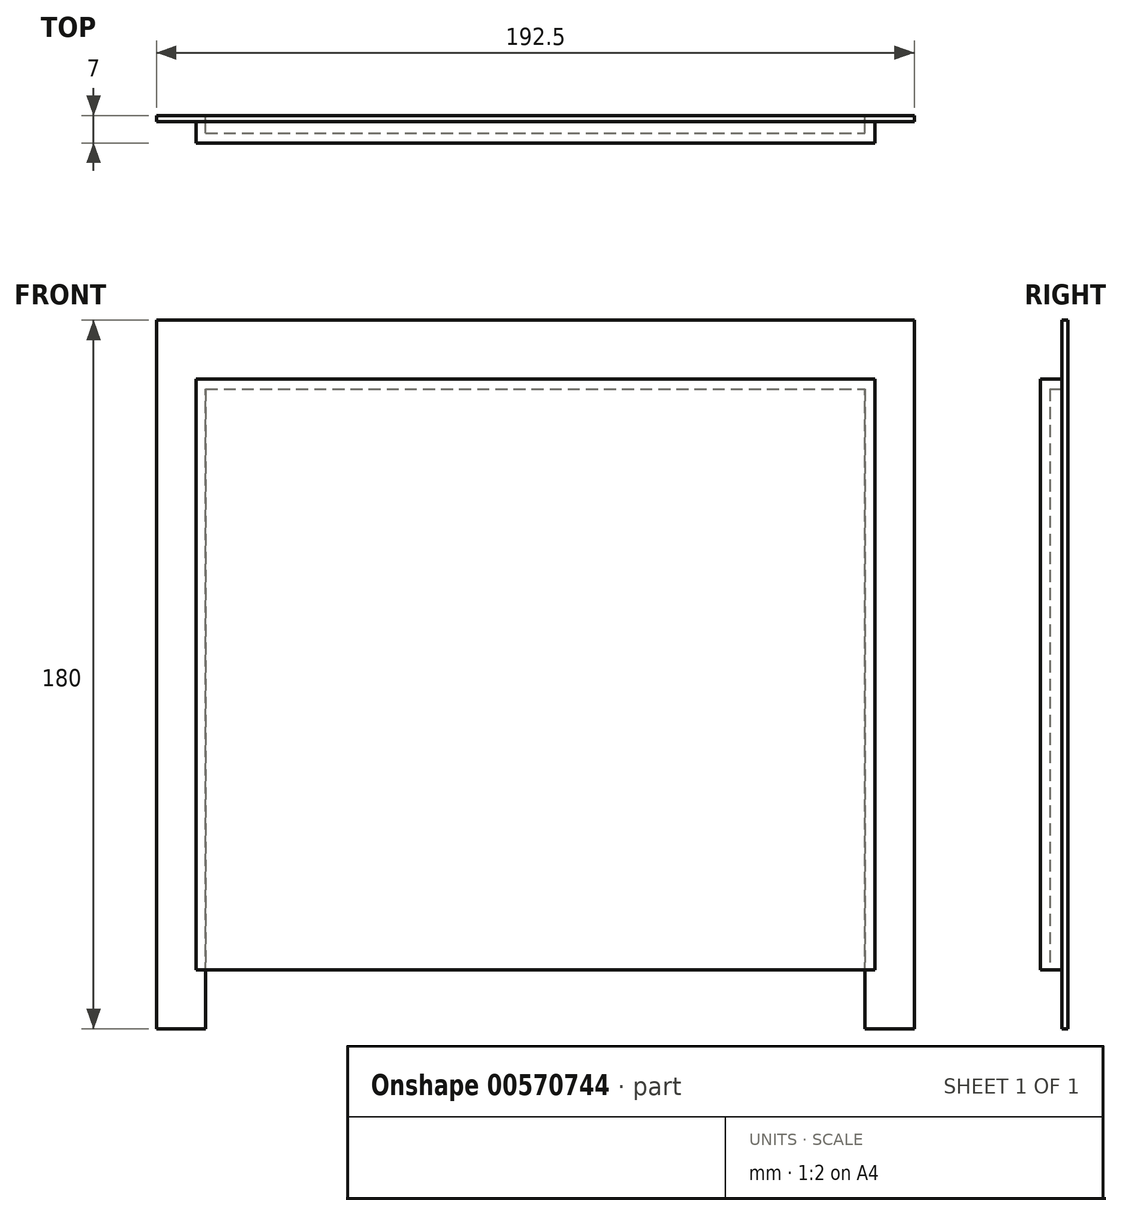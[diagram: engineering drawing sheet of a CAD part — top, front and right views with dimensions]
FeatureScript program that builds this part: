
annotation { "Feature Type Name" : "Feature", "Feature Type Description" : "" }
export const myFeature = defineFeature(function(context is Context, id is Id, definition is map)
    precondition{}
    {
        {
            var Q0;
            Q0=qCreatedBy(makeId("Front.planeOp"),FACE);
            var sketch = newSketch(context, id + "F0", { "sketchPlane" : qUnion([Q0])});
            skLineSegment(sketch, "E0.bottom", {"start": v(96.25, 90) * mm, "end": v(-96.25, 90) * mm});
            skLineSegment(sketch, "E0.top", {"start": v(96.25, -90) * mm, "end": v(-96.25, -90) * mm});
            skLineSegment(sketch, "E0.left", {"start": v(96.25, 90) * mm, "end": v(96.25, -90) * mm});
            skLineSegment(sketch, "E0.right", {"start": v(-96.25, 90) * mm, "end": v(-96.25, -90) * mm});
            skPoint(sketch, "E0.middle", {"position": v(0, 0) * mm});
            skSolve(sketch);
        }
        {
            var Q0;
            Q0=makeQuery(id+"F0.imprint","IMPRINT",FACE,{"disambiguationData":[TD([[makeQuery(id+"F0.imprint","IMPRINT",EDGE,{"derivedFrom":sQuery(id+"F0.wireOp",EDGE,"E0.bottom")}),1.0]])]});
            extrude(context, id + "F1", {"entities" : qUnion([Q0]), "depth" : 1.5 * mm, "offsetDistance" : 25 * mm});
        }
        {
            var Q0;
            Q0=makeQuery(id+"F1.opExtrude","CAP_FACE",FACE,{"disambiguationData":[OSD([sQuery(id+"F0.wireOp",EDGE,"E0.bottom"),sQuery(id+"F0.wireOp",EDGE,"E0.top"),sQuery(id+"F0.wireOp",EDGE,"E0.left"),sQuery(id+"F0.wireOp",EDGE,"E0.right")])],"isStart":false});
            var sketch = newSketch(context, id + "F2", { "sketchPlane" : qUnion([Q0])});
            skLineSegment(sketch, "E1.bottom", {"start": v(86.25, 75) * mm, "end": v(-86.25, 75) * mm});
            skLineSegment(sketch, "E1.top", {"start": v(86.25, -75) * mm, "end": v(-86.25, -75) * mm});
            skLineSegment(sketch, "E1.left", {"start": v(86.25, 75) * mm, "end": v(86.25, -75) * mm});
            skLineSegment(sketch, "E1.right", {"start": v(-86.25, 75) * mm, "end": v(-86.25, -75) * mm});
            skPoint(sketch, "E1.middle", {"position": v(0, 0) * mm});
            skSolve(sketch);
        }
        {
            var Q0;
            Q0 = qSketchRegion(id + "F2", true);
            extrude(context, id + "F3", {"entities" : qUnion([Q0]), "operationType" : NewBodyOperationType.ADD, "depth" : 5.5 * mm, "offsetDistance" : 25 * mm});
        }
        {
            var Q0;
            Q0=makeQuery(id+"F1.opExtrude","CAP_FACE",FACE,{"disambiguationData":[OSD([sQuery(id+"F0.wireOp",EDGE,"E0.bottom"),sQuery(id+"F0.wireOp",EDGE,"E0.top"),sQuery(id+"F0.wireOp",EDGE,"E0.left"),sQuery(id+"F0.wireOp",EDGE,"E0.right")])],"isStart":true});
            shell(context, id + "F4", {"entities" : qUnion([Q0]), "thickness" : 2.5 * mm});
        }
        {
            var Q0;
            Q0=makeQuery(id+"F4.opShell","OFFSET_EDGE",EDGE,{"disambiguationData":[OSD([sQuery(id+"F2.wireOp",EDGE,"E1.top")])]});
            var Q1;
            Q1=makeQuery(id+"F4.opShell","OFFSET_EDGE",EDGE,{"disambiguationData":[OSD([sQuery(id+"F2.wireOp",EDGE,"E1.top"),sQuery(id+"F2.wireOp",EDGE,"E1.left")])]});
            cPlane(context, id + "F5", {"entities" : qUnion([Q0, Q1]), "cplaneType" : CPlaneType.LINE_ANGLE, "offset" : 25 * mm, "angle" : 0 * degree, "width" : 150 * mm, "height" : 150 * mm});
        }
        {
            var Q0;
            Q0=qCreatedBy(id+"F5.planeOp",FACE);
            var sketch = newSketch(context, id + "F6", { "sketchPlane" : qUnion([Q0])});
            skLineSegment(sketch, "E2.bottom", {"start": v(83.75, 0) * mm, "end": v(-83.75, 0) * mm});
            skLineSegment(sketch, "E2.top", {"start": v(83.75, 4.5) * mm, "end": v(-83.75, 4.5) * mm});
            skLineSegment(sketch, "E2.left", {"start": v(83.75, 0) * mm, "end": v(83.75, 4.5) * mm});
            skLineSegment(sketch, "E2.right", {"start": v(-83.75, 0) * mm, "end": v(-83.75, 4.5) * mm});
            skSolve(sketch);
        }
        {
            var Q0;
            Q0 = qSketchRegion(id + "F6", true);
            extrude(context, id + "F7", {"entities" : qUnion([Q0]), "operationType" : NewBodyOperationType.REMOVE, "endBound" : BoundingType.THROUGH_ALL, "depth" : 25 * mm, "offsetDistance" : 25 * mm});
        }
    });
